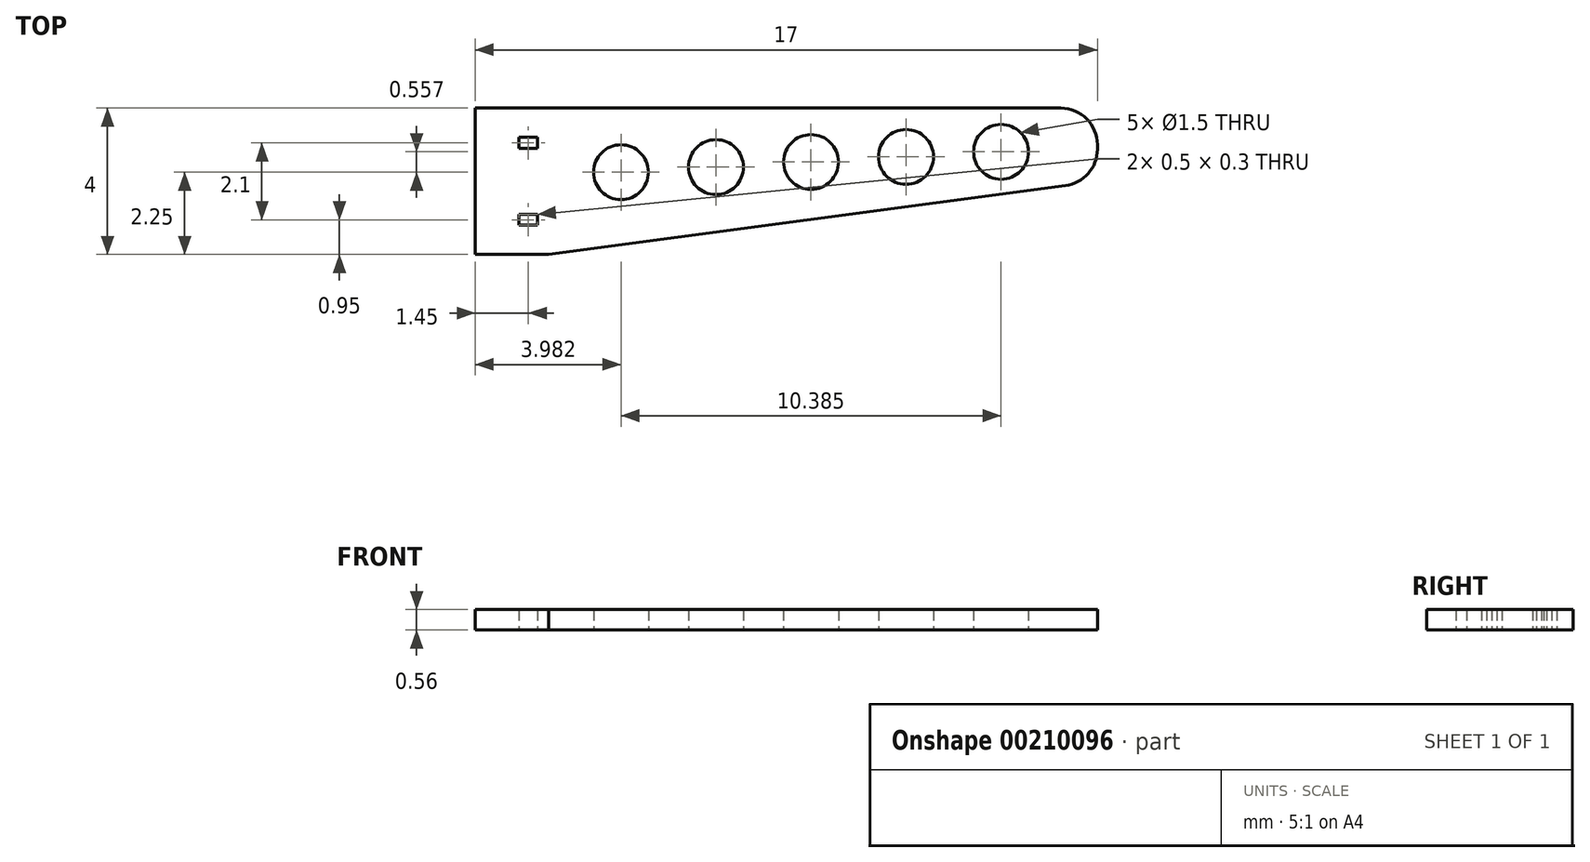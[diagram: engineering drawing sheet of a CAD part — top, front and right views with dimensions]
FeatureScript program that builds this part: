
annotation { "Feature Type Name" : "Feature", "Feature Type Description" : "" }
export const myFeature = defineFeature(function(context is Context, id is Id, definition is map)
    precondition{}
    {
        {
            var Q0;
            Q0=qCreatedBy(makeId("Top.planeOp"),FACE);
            var sketch = newSketch(context, id + "F0", { "sketchPlane" : qUnion([Q0])});
            skLineSegment(sketch, "E0", {"start": v(0, 4) * mm, "end": v(14, 4) * mm});
            skLineSegment(sketch, "E1", {"start": v(15, 3) * mm, "end": v(15, 2.88) * mm});
            skLineSegment(sketch, "E2", {"start": v(14.13, 1.88) * mm, "end": v(0, 0) * mm});
            skCircle(sketch, "E3", {"center": v(12.37, 2.8) * mm, "radius": 0.75 * mm});
            skPoint(sketch, "E4.visualSharp", {"position": v(15, 4) * mm});
            skArc(sketch, "E4.filletArc", {"start": v(15, 3) * mm, "mid": v(14.7, 3.7) * mm, "end": v(14, 4) * mm});
            skPoint(sketch, "E5.visualSharp", {"position": v(15, 2) * mm});
            skArc(sketch, "E5.filletArc", {"start": v(14.13, 1.88) * mm, "mid": v(14.75, 2.22) * mm, "end": v(15, 2.88) * mm});
            skLineSegment(sketch, "E6.bottom", {"start": v(0, 0) * mm, "end": v(-2, 0) * mm});
            skLineSegment(sketch, "E6.top", {"start": v(0, 4) * mm, "end": v(-2, 4) * mm});
            skLineSegment(sketch, "E6.right", {"start": v(-2, 0) * mm, "end": v(-2, 4) * mm});
            skCircle(sketch, "E7.1.0.0", {"center": v(9.77, 2.67) * mm, "radius": 0.75 * mm});
            skCircle(sketch, "E7.2.0.0", {"center": v(7.17, 2.53) * mm, "radius": 0.75 * mm});
            skCircle(sketch, "E7.3.0.0", {"center": v(4.58, 2.39) * mm, "radius": 0.75 * mm});
            skCircle(sketch, "E7.4.0.0", {"center": v(1.98, 2.25) * mm, "radius": 0.75 * mm});
            skLineSegment(sketch, "E8.bottom", {"start": v(-0.3, 0.8) * mm, "end": v(-0.8, 0.8) * mm});
            skLineSegment(sketch, "E8.top", {"start": v(-0.3, 1.1) * mm, "end": v(-0.8, 1.1) * mm});
            skLineSegment(sketch, "E8.left", {"start": v(-0.3, 0.8) * mm, "end": v(-0.3, 1.1) * mm});
            skLineSegment(sketch, "E8.right", {"start": v(-0.8, 0.8) * mm, "end": v(-0.8, 1.1) * mm});
            skLineSegment(sketch, "E9", {"start": v(-2, 2) * mm, "end": v(0, 2) * mm, "construction": true});
            skLineSegment(sketch, "E10", {"start": v(0, 2) * mm, "end": v(15, 2.94) * mm, "construction": true});
            skLineSegment(sketch, "E11.MirrorCS", {"start": v(-0.8, 3.2) * mm, "end": v(-0.8, 2.9) * mm});
            skLineSegment(sketch, "E12.MirrorCS", {"start": v(-0.3, 2.9) * mm, "end": v(-0.8, 2.9) * mm});
            skLineSegment(sketch, "E13.MirrorCS", {"start": v(-0.3, 3.2) * mm, "end": v(-0.3, 2.9) * mm});
            skLineSegment(sketch, "E14.MirrorCS", {"start": v(-0.3, 3.2) * mm, "end": v(-0.8, 3.2) * mm});
            skSolve(sketch);
        }
        {
            var Q0;
            Q0=makeQuery(id+"F0.imprint","IMPRINT",FACE,{"disambiguationData":[TD([[makeQuery(id+"F0.imprint","IMPRINT",EDGE,{"derivedFrom":sQuery(id+"F0.wireOp",EDGE,"E0")}),-1.0]])]});
            extrude(context, id + "F1", {"entities" : qUnion([Q0]), "depth" : .56 * mm});
        }
    });
